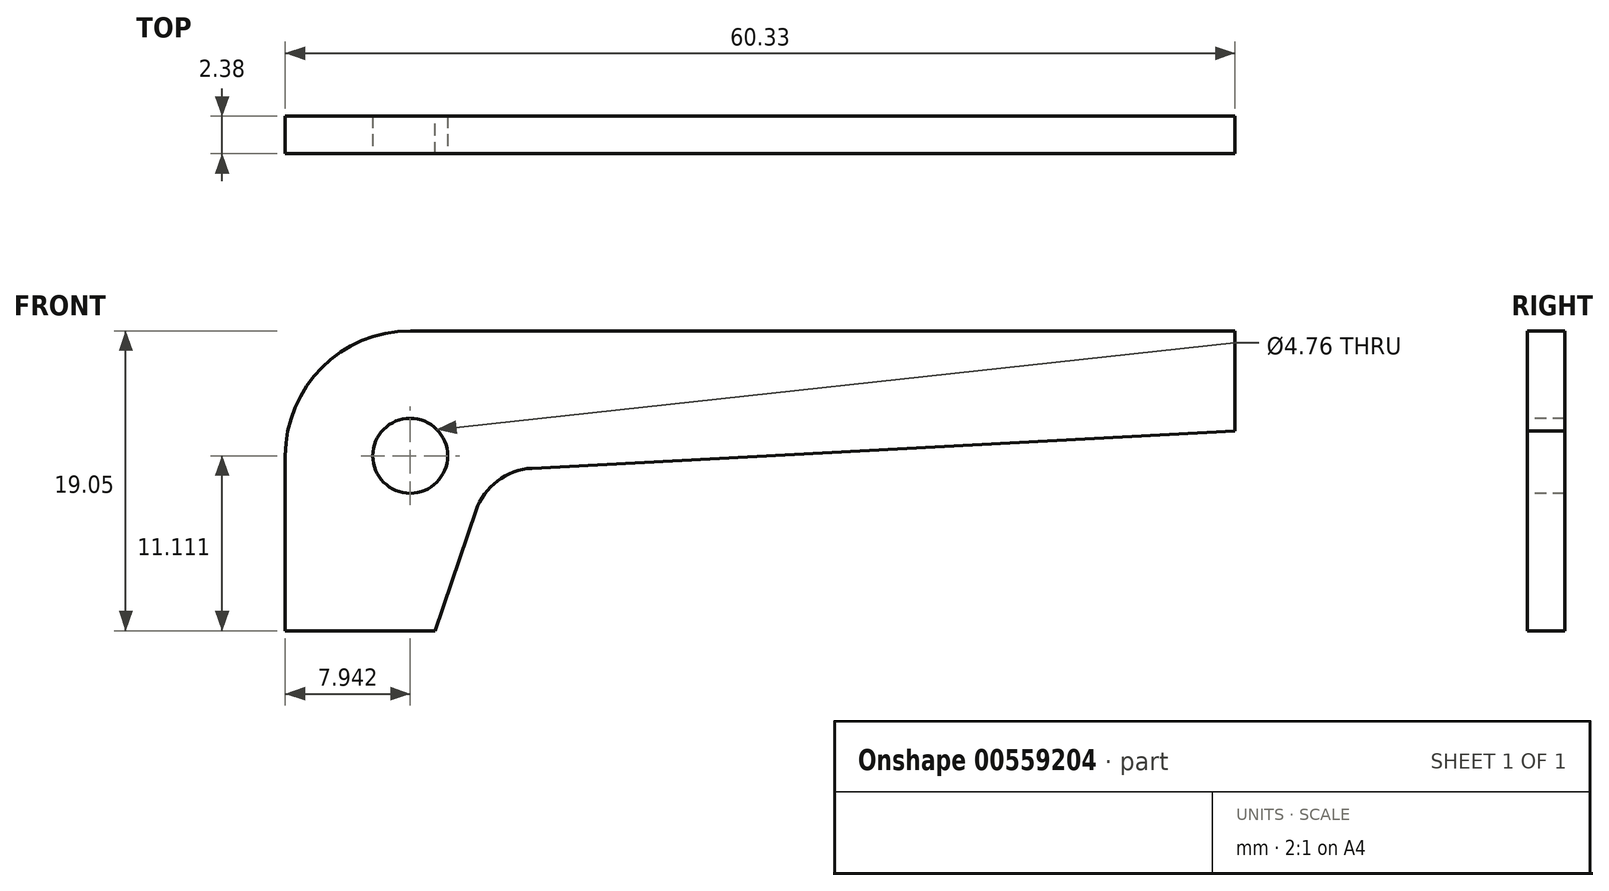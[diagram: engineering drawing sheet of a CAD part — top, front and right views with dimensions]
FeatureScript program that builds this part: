
annotation { "Feature Type Name" : "Feature", "Feature Type Description" : "" }
export const myFeature = defineFeature(function(context is Context, id is Id, definition is map)
    precondition{}
    {
        {
            var Q0;
            Q0=qCreatedBy(makeId("Front.planeOp"),FACE);
            var sketch = newSketch(context, id + "F0", { "sketchPlane" : qUnion([Q0])});
            skLineSegment(sketch, "E0.bottom", {"start": v(14.53, 27.5) * mm, "end": v(66.9, 27.5) * mm});
            skLineSegment(sketch, "E0.left", {"start": v(6.58, 19.55) * mm, "end": v(6.58, 8.45) * mm});
            skLineSegment(sketch, "E1", {"start": v(16.1, 8.45) * mm, "end": v(18.7, 16.08) * mm});
            skLineSegment(sketch, "E2", {"start": v(66.9, 21.15) * mm, "end": v(22.25, 18.77) * mm});
            skLineSegment(sketch, "E3", {"start": v(16.1, 8.45) * mm, "end": v(6.58, 8.45) * mm});
            skLineSegment(sketch, "E4", {"start": v(66.9, 27.5) * mm, "end": v(66.9, 21.15) * mm});
            skArc(sketch, "E5", {"start": v(22.25, 18.77) * mm, "mid": v(20.06, 17.97) * mm, "end": v(18.7, 16.08) * mm});
            skPoint(sketch, "E6.visualSharp", {"position": v(6.58, 27.5) * mm});
            skArc(sketch, "E6.filletArc", {"start": v(14.53, 27.5) * mm, "mid": v(8.91, 25.17) * mm, "end": v(6.58, 19.55) * mm});
            skSolve(sketch);
        }
        {
            var Q0;
            Q0 = qSketchRegion(id + "F0", true);
            extrude(context, id + "F1", {"entities" : qUnion([Q0]), "depth" : 2.38 * mm, "offsetDistance" : 25.4 * mm});
        }
        {
            var Q0;
            Q0=makeQuery(id+"F1.opExtrude","CAP_FACE",FACE,{"disambiguationData":[OSD([sQuery(id+"F0.wireOp",EDGE,"E0.bottom"),sQuery(id+"F0.wireOp",EDGE,"E0.left"),sQuery(id+"F0.wireOp",EDGE,"E1"),sQuery(id+"F0.wireOp",EDGE,"E2"),sQuery(id+"F0.wireOp",EDGE,"E3"),sQuery(id+"F0.wireOp",EDGE,"E4"),sQuery(id+"F0.wireOp",EDGE,"E5"),sQuery(id+"F0.wireOp",EDGE,"E6.filletArc")])],"isStart":false});
            var sketch = newSketch(context, id + "F2", { "sketchPlane" : qUnion([Q0])});
            skCircle(sketch, "E7", {"center": v(14.52, 19.56) * mm, "radius": 2.38 * mm});
            skSolve(sketch);
        }
        {
            var Q0;
            Q0=makeQuery(id+"F2.imprint","IMPRINT",FACE,{"disambiguationData":[TD([[makeQuery(id+"F2.imprint","IMPRINT",EDGE,{"derivedFrom":sQuery(id+"F2.wireOp",EDGE,"E7")}),1.0]])]});
            extrude(context, id + "F3", {"entities" : qUnion([Q0]), "operationType" : NewBodyOperationType.REMOVE, "endBound" : BoundingType.THROUGH_ALL, "oppositeDirection" : true, "depth" : 25.4 * mm, "offsetDistance" : 25.4 * mm});
        }
    });
